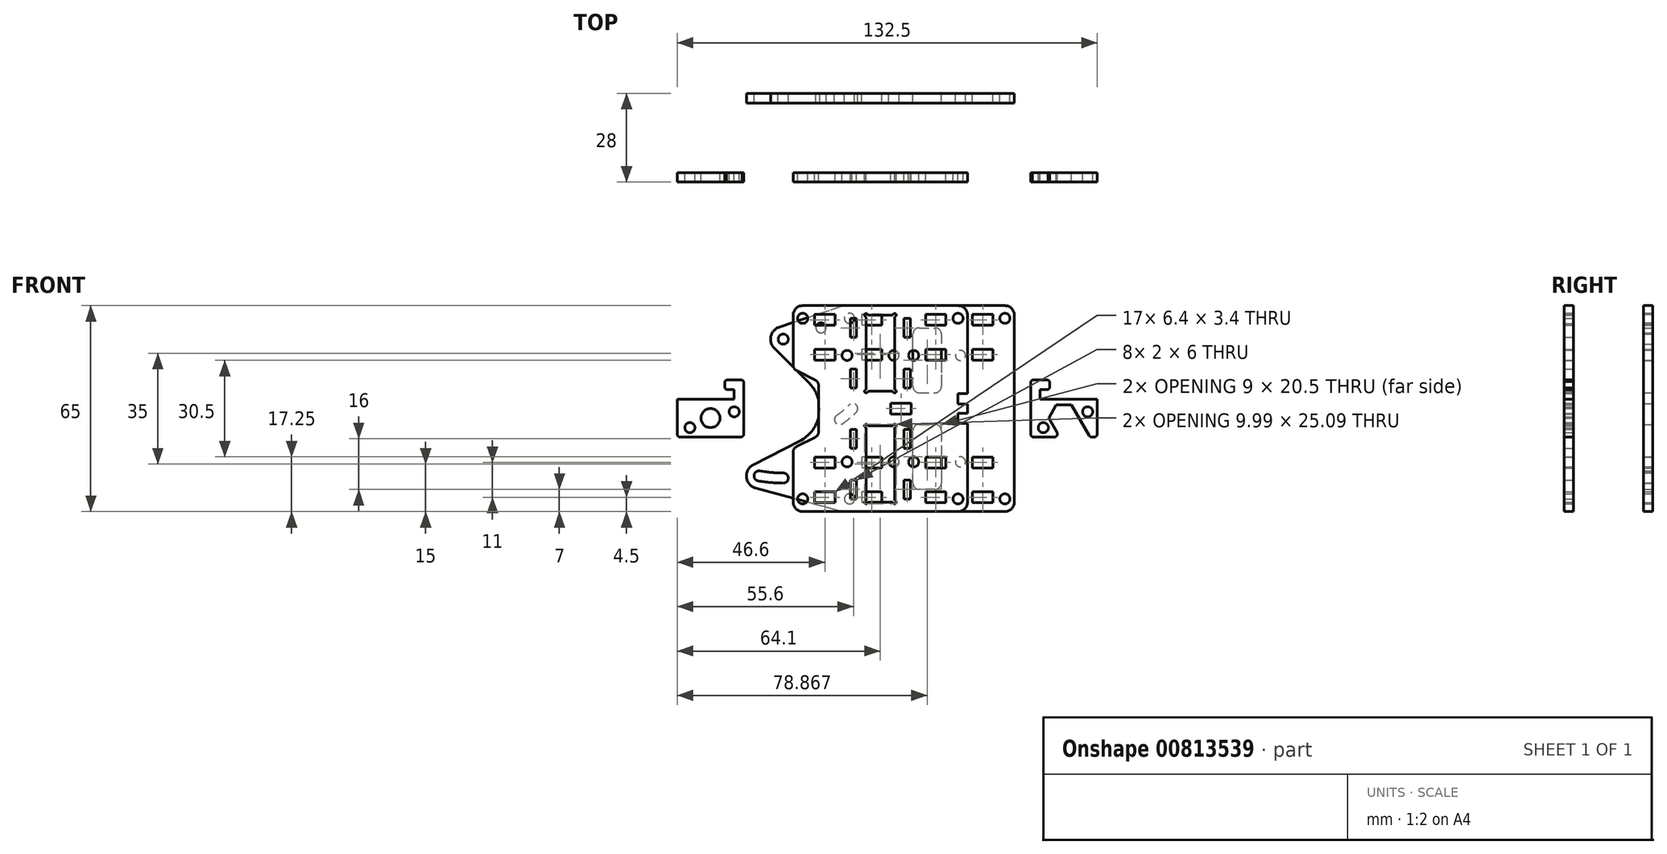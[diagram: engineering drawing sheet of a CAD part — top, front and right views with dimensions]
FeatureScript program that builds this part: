
annotation { "Feature Type Name" : "Feature", "Feature Type Description" : "" }
export const myFeature = defineFeature(function(context is Context, id is Id, definition is map)
    precondition{}
    {
        {
            var Q0;
            Q0=qCreatedBy(makeId("Front.planeOp"),FACE);
            var sketch = newSketch(context, id + "F0", { "sketchPlane" : qUnion([Q0])});
            skLineSegment(sketch, "E0", {"start": v(-7.5, 12.5) * mm, "end": v(-9.5, 12.5) * mm});
            skLineSegment(sketch, "E1", {"start": v(9.5, 12.5) * mm, "end": v(7.5, 12.5) * mm});
            skLineSegment(sketch, "E2", {"start": v(-9.5, -12.5) * mm, "end": v(-7.5, -12.5) * mm});
            skLineSegment(sketch, "E3", {"start": v(7.5, -12.5) * mm, "end": v(9.5, -12.5) * mm});
            skLineSegment(sketch, "E4", {"start": v(-7.5, -22.5) * mm, "end": v(-9.5, -22.5) * mm});
            skLineSegment(sketch, "E5", {"start": v(9.5, -22.5) * mm, "end": v(7.5, -22.5) * mm});
            skLineSegment(sketch, "E6", {"start": v(-9.5, 22.5) * mm, "end": v(-7.5, 22.5) * mm});
            skLineSegment(sketch, "E7", {"start": v(7.5, 22.5) * mm, "end": v(9.5, 22.5) * mm});
            skLineSegment(sketch, "E8", {"start": v(27.5, 1.5) * mm, "end": v(27.5, -1.5) * mm});
            skArc(sketch, "E9", {"start": v(4.75, 29.12) * mm, "mid": v(4.85, 29.9) * mm, "end": v(4.07, 29.8) * mm});
            skArc(sketch, "E10", {"start": v(3.63, 29.55) * mm, "mid": v(3.88, 29.62) * mm, "end": v(4.07, 29.8) * mm});
            skArc(sketch, "E11", {"start": v(4.75, 29.12) * mm, "mid": v(4.57, 28.93) * mm, "end": v(4.5, 28.68) * mm});
            skLineSegment(sketch, "E12", {"start": v(4.5, 6.32) * mm, "end": v(4.5, 28.68) * mm});
            skArc(sketch, "E13", {"start": v(4.5, 6.32) * mm, "mid": v(4.57, 6.07) * mm, "end": v(4.75, 5.88) * mm});
            skArc(sketch, "E14", {"start": v(4.07, 5.2) * mm, "mid": v(4.85, 5.1) * mm, "end": v(4.75, 5.88) * mm});
            skArc(sketch, "E15", {"start": v(4.07, 5.2) * mm, "mid": v(3.88, 5.38) * mm, "end": v(3.63, 5.45) * mm});
            skLineSegment(sketch, "E16", {"start": v(-3.63, 5.45) * mm, "end": v(3.63, 5.45) * mm});
            skArc(sketch, "E17", {"start": v(-3.63, 5.45) * mm, "mid": v(-3.88, 5.38) * mm, "end": v(-4.07, 5.2) * mm});
            skArc(sketch, "E18", {"start": v(-4.75, 5.88) * mm, "mid": v(-4.85, 5.1) * mm, "end": v(-4.07, 5.2) * mm});
            skArc(sketch, "E19", {"start": v(-4.75, 5.88) * mm, "mid": v(-4.57, 6.07) * mm, "end": v(-4.5, 6.32) * mm});
            skLineSegment(sketch, "E20", {"start": v(-4.5, 28.68) * mm, "end": v(-4.5, 6.32) * mm});
            skArc(sketch, "E21", {"start": v(-4.5, 28.68) * mm, "mid": v(-4.57, 28.93) * mm, "end": v(-4.75, 29.12) * mm});
            skArc(sketch, "E22", {"start": v(-4.07, 29.8) * mm, "mid": v(-4.85, 29.9) * mm, "end": v(-4.75, 29.12) * mm});
            skArc(sketch, "E23", {"start": v(-4.07, 29.8) * mm, "mid": v(-3.88, 29.62) * mm, "end": v(-3.63, 29.55) * mm});
            skLineSegment(sketch, "E24", {"start": v(3.63, 29.55) * mm, "end": v(-3.63, 29.55) * mm});
            skArc(sketch, "E25", {"start": v(4.75, -5.88) * mm, "mid": v(4.85, -5.1) * mm, "end": v(4.07, -5.2) * mm});
            skArc(sketch, "E26", {"start": v(3.63, -5.45) * mm, "mid": v(3.88, -5.38) * mm, "end": v(4.07, -5.2) * mm});
            skArc(sketch, "E27", {"start": v(4.75, -5.88) * mm, "mid": v(4.57, -6.07) * mm, "end": v(4.5, -6.32) * mm});
            skLineSegment(sketch, "E28", {"start": v(4.5, -28.68) * mm, "end": v(4.5, -6.32) * mm});
            skArc(sketch, "E29", {"start": v(4.5, -28.68) * mm, "mid": v(4.57, -28.93) * mm, "end": v(4.75, -29.12) * mm});
            skArc(sketch, "E30", {"start": v(4.07, -29.8) * mm, "mid": v(4.85, -29.9) * mm, "end": v(4.75, -29.12) * mm});
            skArc(sketch, "E31", {"start": v(4.07, -29.8) * mm, "mid": v(3.88, -29.62) * mm, "end": v(3.63, -29.55) * mm});
            skLineSegment(sketch, "E32", {"start": v(-3.63, -29.55) * mm, "end": v(3.63, -29.55) * mm});
            skArc(sketch, "E33", {"start": v(-3.63, -29.55) * mm, "mid": v(-3.88, -29.62) * mm, "end": v(-4.07, -29.8) * mm});
            skArc(sketch, "E34", {"start": v(-4.75, -29.12) * mm, "mid": v(-4.85, -29.9) * mm, "end": v(-4.07, -29.8) * mm});
            skArc(sketch, "E35", {"start": v(-4.75, -29.12) * mm, "mid": v(-4.57, -28.93) * mm, "end": v(-4.5, -28.68) * mm});
            skLineSegment(sketch, "E36", {"start": v(-4.5, -6.32) * mm, "end": v(-4.5, -28.68) * mm});
            skArc(sketch, "E37", {"start": v(-4.5, -6.32) * mm, "mid": v(-4.57, -6.07) * mm, "end": v(-4.75, -5.88) * mm});
            skArc(sketch, "E38", {"start": v(-4.07, -5.2) * mm, "mid": v(-4.85, -5.1) * mm, "end": v(-4.75, -5.88) * mm});
            skArc(sketch, "E39", {"start": v(-4.07, -5.2) * mm, "mid": v(-3.88, -5.38) * mm, "end": v(-3.63, -5.45) * mm});
            skLineSegment(sketch, "E40", {"start": v(3.63, -5.45) * mm, "end": v(-3.63, -5.45) * mm});
            skLineSegment(sketch, "E41", {"start": v(24.4, 1.5) * mm, "end": v(27.5, 1.5) * mm});
            skLineSegment(sketch, "E42", {"start": v(27.5, -1.5) * mm, "end": v(24.4, -1.5) * mm});
            skLineSegment(sketch, "E43", {"start": v(27.5, 4.7) * mm, "end": v(24.4, 4.7) * mm});
            skLineSegment(sketch, "E44", {"start": v(24.4, 4.7) * mm, "end": v(24.4, 1.5) * mm});
            skLineSegment(sketch, "E45", {"start": v(24.4, -4.7) * mm, "end": v(27.5, -4.7) * mm});
            skLineSegment(sketch, "E46", {"start": v(24.4, -1.5) * mm, "end": v(24.4, -4.7) * mm});
            skLineSegment(sketch, "E47", {"start": v(9.7, -1.7) * mm, "end": v(9.7, 1.7) * mm});
            skLineSegment(sketch, "E48", {"start": v(9.7, 1.7) * mm, "end": v(3.3, 1.7) * mm});
            skLineSegment(sketch, "E49", {"start": v(9.7, -1.7) * mm, "end": v(3.3, -1.7) * mm});
            skLineSegment(sketch, "E50", {"start": v(3.3, 1.7) * mm, "end": v(3.3, -1.7) * mm});
            skLineSegment(sketch, "E51", {"start": v(9.5, 28.5) * mm, "end": v(7.5, 28.5) * mm});
            skLineSegment(sketch, "E52", {"start": v(7.5, 6.5) * mm, "end": v(9.5, 6.5) * mm});
            skLineSegment(sketch, "E53", {"start": v(9.5, -6.5) * mm, "end": v(7.5, -6.5) * mm});
            skLineSegment(sketch, "E54", {"start": v(7.5, -28.5) * mm, "end": v(9.5, -28.5) * mm});
            skLineSegment(sketch, "E55", {"start": v(-7.5, 28.5) * mm, "end": v(-9.5, 28.5) * mm});
            skLineSegment(sketch, "E56", {"start": v(-9.5, 6.5) * mm, "end": v(-7.5, 6.5) * mm});
            skLineSegment(sketch, "E57", {"start": v(-7.5, -6.5) * mm, "end": v(-9.5, -6.5) * mm});
            skLineSegment(sketch, "E58", {"start": v(-9.5, -28.5) * mm, "end": v(-7.5, -28.5) * mm});
            skLineSegment(sketch, "E59", {"start": v(9.5, 22.5) * mm, "end": v(9.5, 28.5) * mm});
            skLineSegment(sketch, "E60", {"start": v(7.5, 28.5) * mm, "end": v(7.5, 22.5) * mm});
            skLineSegment(sketch, "E61", {"start": v(9.5, 6.5) * mm, "end": v(9.5, 12.5) * mm});
            skLineSegment(sketch, "E62", {"start": v(7.5, 12.5) * mm, "end": v(7.5, 6.5) * mm});
            skLineSegment(sketch, "E63", {"start": v(9.5, -12.5) * mm, "end": v(9.5, -6.5) * mm});
            skLineSegment(sketch, "E64", {"start": v(7.5, -6.5) * mm, "end": v(7.5, -12.5) * mm});
            skLineSegment(sketch, "E65", {"start": v(9.5, -28.5) * mm, "end": v(9.5, -22.5) * mm});
            skLineSegment(sketch, "E66", {"start": v(7.5, -22.5) * mm, "end": v(7.5, -28.5) * mm});
            skLineSegment(sketch, "E67", {"start": v(-7.5, 22.5) * mm, "end": v(-7.5, 28.5) * mm});
            skLineSegment(sketch, "E68", {"start": v(-9.5, 28.5) * mm, "end": v(-9.5, 22.5) * mm});
            skLineSegment(sketch, "E69", {"start": v(-7.5, 6.5) * mm, "end": v(-7.5, 12.5) * mm});
            skLineSegment(sketch, "E70", {"start": v(-9.5, 12.5) * mm, "end": v(-9.5, 6.5) * mm});
            skLineSegment(sketch, "E71", {"start": v(-7.5, -12.5) * mm, "end": v(-7.5, -6.5) * mm});
            skLineSegment(sketch, "E72", {"start": v(-9.5, -6.5) * mm, "end": v(-9.5, -12.5) * mm});
            skLineSegment(sketch, "E73", {"start": v(-7.5, -28.5) * mm, "end": v(-7.5, -22.5) * mm});
            skLineSegment(sketch, "E74", {"start": v(-9.5, -22.5) * mm, "end": v(-9.5, -28.5) * mm});
            skLineSegment(sketch, "E75", {"start": v(-14.3, 26.3) * mm, "end": v(-14.3, 29.7) * mm});
            skLineSegment(sketch, "E76", {"start": v(-14.3, 29.7) * mm, "end": v(-20.7, 29.7) * mm});
            skLineSegment(sketch, "E77", {"start": v(-14.3, 26.3) * mm, "end": v(-20.7, 26.3) * mm});
            skLineSegment(sketch, "E78", {"start": v(-20.7, 29.7) * mm, "end": v(-20.7, 26.3) * mm});
            skLineSegment(sketch, "E79", {"start": v(-14.3, 15.3) * mm, "end": v(-14.3, 18.7) * mm});
            skLineSegment(sketch, "E80", {"start": v(-14.3, 18.7) * mm, "end": v(-20.7, 18.7) * mm});
            skLineSegment(sketch, "E81", {"start": v(-14.3, 15.3) * mm, "end": v(-20.7, 15.3) * mm});
            skLineSegment(sketch, "E82", {"start": v(-20.7, 18.7) * mm, "end": v(-20.7, 15.3) * mm});
            skLineSegment(sketch, "E83", {"start": v(-14.3, -18.7) * mm, "end": v(-14.3, -15.3) * mm});
            skLineSegment(sketch, "E84", {"start": v(-14.3, -15.3) * mm, "end": v(-20.7, -15.3) * mm});
            skLineSegment(sketch, "E85", {"start": v(-14.3, -18.7) * mm, "end": v(-20.7, -18.7) * mm});
            skLineSegment(sketch, "E86", {"start": v(-20.7, -15.3) * mm, "end": v(-20.7, -18.7) * mm});
            skLineSegment(sketch, "E87", {"start": v(-14.3, -29.7) * mm, "end": v(-14.3, -26.3) * mm});
            skLineSegment(sketch, "E88", {"start": v(-14.3, -26.3) * mm, "end": v(-20.7, -26.3) * mm});
            skLineSegment(sketch, "E89", {"start": v(-14.3, -29.7) * mm, "end": v(-20.7, -29.7) * mm});
            skLineSegment(sketch, "E90", {"start": v(-20.7, -26.3) * mm, "end": v(-20.7, -29.7) * mm});
            skCircle(sketch, "E91", {"center": v(-24.5, 28.5) * mm, "radius": 1.6 * mm});
            skCircle(sketch, "E92", {"center": v(-24.5, -28.5) * mm, "radius": 1.6 * mm});
            skLineSegment(sketch, "E93", {"start": v(20.7, 26.3) * mm, "end": v(20.7, 29.7) * mm});
            skLineSegment(sketch, "E94", {"start": v(20.7, 29.7) * mm, "end": v(14.3, 29.7) * mm});
            skLineSegment(sketch, "E95", {"start": v(20.7, 26.3) * mm, "end": v(14.3, 26.3) * mm});
            skLineSegment(sketch, "E96", {"start": v(14.3, 29.7) * mm, "end": v(14.3, 26.3) * mm});
            skLineSegment(sketch, "E97", {"start": v(20.7, 15.3) * mm, "end": v(20.7, 18.7) * mm});
            skLineSegment(sketch, "E98", {"start": v(20.7, 18.7) * mm, "end": v(14.3, 18.7) * mm});
            skLineSegment(sketch, "E99", {"start": v(20.7, 15.3) * mm, "end": v(14.3, 15.3) * mm});
            skLineSegment(sketch, "E100", {"start": v(14.3, 18.7) * mm, "end": v(14.3, 15.3) * mm});
            skLineSegment(sketch, "E101", {"start": v(20.7, -18.7) * mm, "end": v(20.7, -15.3) * mm});
            skLineSegment(sketch, "E102", {"start": v(20.7, -15.3) * mm, "end": v(14.3, -15.3) * mm});
            skLineSegment(sketch, "E103", {"start": v(20.7, -18.7) * mm, "end": v(14.3, -18.7) * mm});
            skLineSegment(sketch, "E104", {"start": v(14.3, -15.3) * mm, "end": v(14.3, -18.7) * mm});
            skLineSegment(sketch, "E105", {"start": v(20.7, -29.7) * mm, "end": v(20.7, -26.3) * mm});
            skLineSegment(sketch, "E106", {"start": v(20.7, -26.3) * mm, "end": v(14.3, -26.3) * mm});
            skLineSegment(sketch, "E107", {"start": v(20.7, -29.7) * mm, "end": v(14.3, -29.7) * mm});
            skLineSegment(sketch, "E108", {"start": v(14.3, -26.3) * mm, "end": v(14.3, -29.7) * mm});
            skCircle(sketch, "E109", {"center": v(24.5, 28.5) * mm, "radius": 1.6 * mm});
            skCircle(sketch, "E110", {"center": v(24.5, -28.5) * mm, "radius": 1.6 * mm});
            skLineSegment(sketch, "E111", {"start": v(27.5, -4.7) * mm, "end": v(27.5, -29.5) * mm});
            skArc(sketch, "E112", {"start": v(24.5, -32.5) * mm, "mid": v(26.62, -31.62) * mm, "end": v(27.5, -29.5) * mm});
            skArc(sketch, "E113", {"start": v(27.5, 29.5) * mm, "mid": v(26.62, 31.62) * mm, "end": v(24.5, 32.5) * mm});
            skCircle(sketch, "E114", {"center": v(-10.5, 16.8) * mm, "radius": 1.6 * mm});
            skCircle(sketch, "E115", {"center": v(10.5, 16.8) * mm, "radius": 1.6 * mm});
            skCircle(sketch, "E116", {"center": v(10.5, -16.8) * mm, "radius": 1.6 * mm});
            skCircle(sketch, "E117", {"center": v(-10.5, -16.8) * mm, "radius": 1.6 * mm});
            skLineSegment(sketch, "E118", {"start": v(-24.5, 32.5) * mm, "end": v(24.5, 32.5) * mm});
            skLineSegment(sketch, "E119", {"start": v(24.5, -32.5) * mm, "end": v(-24.5, -32.5) * mm});
            skArc(sketch, "E120", {"start": v(-27.5, 13.74) * mm, "mid": v(-27.2, 12.68) * mm, "end": v(-26.4, 11.95) * mm});
            skLineSegment(sketch, "E121", {"start": v(-26.4, 11.95) * mm, "end": v(-20.6, 9.05) * mm});
            skArc(sketch, "E122", {"start": v(-19.5, 7.26) * mm, "mid": v(-19.8, 8.32) * mm, "end": v(-20.6, 9.05) * mm});
            skLineSegment(sketch, "E123", {"start": v(-19.5, 7.26) * mm, "end": v(-19.5, -7.26) * mm});
            skArc(sketch, "E124", {"start": v(-20.6, -9.05) * mm, "mid": v(-19.8, -8.32) * mm, "end": v(-19.5, -7.26) * mm});
            skLineSegment(sketch, "E125", {"start": v(-20.6, -9.05) * mm, "end": v(-26.4, -11.95) * mm});
            skArc(sketch, "E126", {"start": v(-26.4, -11.95) * mm, "mid": v(-27.2, -12.68) * mm, "end": v(-27.5, -13.74) * mm});
            skLineSegment(sketch, "E127", {"start": v(-27.5, 29.5) * mm, "end": v(-27.5, 13.74) * mm});
            skArc(sketch, "E128", {"start": v(-24.5, 32.5) * mm, "mid": v(-26.62, 31.62) * mm, "end": v(-27.5, 29.5) * mm});
            skLineSegment(sketch, "E129", {"start": v(-27.5, -13.74) * mm, "end": v(-27.5, -29.5) * mm});
            skArc(sketch, "E130", {"start": v(-27.5, -29.5) * mm, "mid": v(-26.62, -31.62) * mm, "end": v(-24.5, -32.5) * mm});
            skLineSegment(sketch, "E131", {"start": v(27.5, 29.5) * mm, "end": v(27.5, 4.7) * mm});
            skSolve(sketch);
        }
        {
            var Q0;
            Q0=makeQuery(id+"F0.imprint","IMPRINT",FACE,{"disambiguationData":[TD([[makeQuery(id+"F0.imprint","IMPRINT",EDGE,{"derivedFrom":sQuery(id+"F0.wireOp",EDGE,"E0")}),-1.0]])]});
            extrude(context, id + "F1", {"entities" : qUnion([Q0]), "depth" : 3 * mm, "offsetDistance" : 25 * mm});
        }
        {
            var Q0;
            Q0=qCreatedBy(makeId("Front.planeOp"),FACE);
            cPlane(context, id + "F2", {"entities" : qUnion([Q0]), "cplaneType" : CPlaneType.OFFSET, "offset" : 25 * mm, "oppositeDirection" : true, "width" : 150 * mm, "height" : 150 * mm});
        }
        {
            var Q0;
            Q0=qCreatedBy(id+"F2.planeOp",FACE);
            var sketch = newSketch(context, id + "F3", { "sketchPlane" : qUnion([Q0])});
            skArc(sketch, "E132", {"start": v(19.27, 23.5) * mm, "mid": v(18.68, 24.91) * mm, "end": v(17.27, 25.5) * mm});
            skLineSegment(sketch, "E133", {"start": v(12.27, 25.5) * mm, "end": v(17.27, 25.5) * mm});
            skArc(sketch, "E134", {"start": v(12.27, 25.5) * mm, "mid": v(10.85, 24.91) * mm, "end": v(10.27, 23.5) * mm});
            skArc(sketch, "E135", {"start": v(17.27, -25.5) * mm, "mid": v(18.68, -24.91) * mm, "end": v(19.27, -23.5) * mm});
            skLineSegment(sketch, "E136", {"start": v(17.27, -25.5) * mm, "end": v(12.27, -25.5) * mm});
            skArc(sketch, "E137", {"start": v(10.27, -23.5) * mm, "mid": v(10.85, -24.91) * mm, "end": v(12.27, -25.5) * mm});
            skLineSegment(sketch, "E138", {"start": v(10.27, 7) * mm, "end": v(10.27, 23.5) * mm});
            skArc(sketch, "E139", {"start": v(10.27, 7) * mm, "mid": v(10.85, 5.59) * mm, "end": v(12.27, 5) * mm});
            skLineSegment(sketch, "E140", {"start": v(19.27, 23.5) * mm, "end": v(19.27, 7) * mm});
            skLineSegment(sketch, "E141", {"start": v(12.27, 5) * mm, "end": v(17.27, 5) * mm});
            skArc(sketch, "E142", {"start": v(17.27, 5) * mm, "mid": v(18.68, 5.59) * mm, "end": v(19.27, 7) * mm});
            skLineSegment(sketch, "E143", {"start": v(10.27, -23.5) * mm, "end": v(10.27, -7) * mm});
            skArc(sketch, "E144", {"start": v(12.27, -5) * mm, "mid": v(10.85, -5.59) * mm, "end": v(10.27, -7) * mm});
            skLineSegment(sketch, "E145", {"start": v(12.27, -5) * mm, "end": v(17.27, -5) * mm});
            skLineSegment(sketch, "E146", {"start": v(19.27, -7) * mm, "end": v(19.27, -23.5) * mm});
            skArc(sketch, "E147", {"start": v(19.27, -7) * mm, "mid": v(18.68, -5.59) * mm, "end": v(17.27, -5) * mm});
            skCircle(sketch, "E148", {"center": v(-9.73, 28.5) * mm, "radius": 1.6 * mm});
            skCircle(sketch, "E149", {"center": v(-9.73, -28.5) * mm, "radius": 1.6 * mm});
            skLineSegment(sketch, "E150", {"start": v(0.47, 26.3) * mm, "end": v(0.47, 29.7) * mm});
            skLineSegment(sketch, "E151", {"start": v(0.47, 29.7) * mm, "end": v(-5.93, 29.7) * mm});
            skLineSegment(sketch, "E152", {"start": v(0.47, 26.3) * mm, "end": v(-5.93, 26.3) * mm});
            skLineSegment(sketch, "E153", {"start": v(-5.93, 29.7) * mm, "end": v(-5.93, 26.3) * mm});
            skLineSegment(sketch, "E154", {"start": v(0.47, 15.3) * mm, "end": v(0.47, 18.7) * mm});
            skLineSegment(sketch, "E155", {"start": v(0.47, 18.7) * mm, "end": v(-5.93, 18.7) * mm});
            skLineSegment(sketch, "E156", {"start": v(0.47, 15.3) * mm, "end": v(-5.93, 15.3) * mm});
            skLineSegment(sketch, "E157", {"start": v(-5.93, 18.7) * mm, "end": v(-5.93, 15.3) * mm});
            skLineSegment(sketch, "E158", {"start": v(0.47, -18.7) * mm, "end": v(0.47, -15.3) * mm});
            skLineSegment(sketch, "E159", {"start": v(0.47, -15.3) * mm, "end": v(-5.93, -15.3) * mm});
            skLineSegment(sketch, "E160", {"start": v(0.47, -18.7) * mm, "end": v(-5.93, -18.7) * mm});
            skLineSegment(sketch, "E161", {"start": v(-5.93, -15.3) * mm, "end": v(-5.93, -18.7) * mm});
            skLineSegment(sketch, "E162", {"start": v(0.47, -29.7) * mm, "end": v(0.47, -26.3) * mm});
            skLineSegment(sketch, "E163", {"start": v(0.47, -26.3) * mm, "end": v(-5.93, -26.3) * mm});
            skLineSegment(sketch, "E164", {"start": v(0.47, -29.7) * mm, "end": v(-5.93, -29.7) * mm});
            skLineSegment(sketch, "E165", {"start": v(-5.93, -26.3) * mm, "end": v(-5.93, -29.7) * mm});
            skCircle(sketch, "E166", {"center": v(-30.65, 21.92) * mm, "radius": 1.6 * mm});
            skArc(sketch, "E167", {"start": v(-7.6, -1.13) * mm, "mid": v(-7.6, 1.13) * mm, "end": v(-9.86, 1.13) * mm});
            skArc(sketch, "E168", {"start": v(-13.8, -2.16) * mm, "mid": v(-11.76, -0.6) * mm, "end": v(-9.86, 1.13) * mm});
            skArc(sketch, "E169", {"start": v(-11.96, -4.78) * mm, "mid": v(-9.7, -3.05) * mm, "end": v(-7.6, -1.13) * mm});
            skArc(sketch, "E170", {"start": v(-13.8, -2.16) * mm, "mid": v(-14.18, -4.4) * mm, "end": v(-11.96, -4.78) * mm});
            skArc(sketch, "E171", {"start": v(-37.99, -19.68) * mm, "mid": v(-34.34, -20.16) * mm, "end": v(-30.65, -20.32) * mm});
            skArc(sketch, "E172", {"start": v(-30.65, -23.52) * mm, "mid": v(-29.05, -21.92) * mm, "end": v(-30.65, -20.32) * mm});
            skArc(sketch, "E173", {"start": v(-38.54, -22.83) * mm, "mid": v(-34.61, -23.35) * mm, "end": v(-30.65, -23.52) * mm});
            skArc(sketch, "E174", {"start": v(-37.99, -19.68) * mm, "mid": v(-39.84, -20.98) * mm, "end": v(-38.54, -22.83) * mm});
            skCircle(sketch, "E175", {"center": v(-18.73, 25.5) * mm, "radius": 1.6 * mm});
            skLineSegment(sketch, "E176", {"start": v(-33.48, 19.1) * mm, "end": v(-22.52, 8.13) * mm});
            skLineSegment(sketch, "E177", {"start": v(-40.08, -17.69) * mm, "end": v(-25.44, -10.25) * mm});
            skArc(sketch, "E178", {"start": v(-31.93, 25.71) * mm, "mid": v(-34.55, 22.83) * mm, "end": v(-33.48, 19.1) * mm});
            skArc(sketch, "E179", {"start": v(-40.08, -17.69) * mm, "mid": v(-42.24, -21.67) * mm, "end": v(-39.3, -25.12) * mm});
            skArc(sketch, "E180", {"start": v(-25.44, -10.25) * mm, "mid": v(-19.3, -1.8) * mm, "end": v(-22.52, 8.13) * mm});
            skLineSegment(sketch, "E181", {"start": v(-39.3, -25.12) * mm, "end": v(-12.24, -32.36) * mm});
            skArc(sketch, "E182", {"start": v(-12.24, -32.36) * mm, "mid": v(-11.73, -32.47) * mm, "end": v(-11.2, -32.5) * mm});
            skLineSegment(sketch, "E183", {"start": v(-31.93, 25.71) * mm, "end": v(-12.35, 32.3) * mm});
            skArc(sketch, "E184", {"start": v(-11.08, 32.5) * mm, "mid": v(-11.72, 32.45) * mm, "end": v(-12.35, 32.3) * mm});
            skCircle(sketch, "E185", {"center": v(39.27, 28.5) * mm, "radius": 1.6 * mm});
            skCircle(sketch, "E186", {"center": v(39.27, -28.5) * mm, "radius": 1.6 * mm});
            skLineSegment(sketch, "E187", {"start": v(35.47, 26.3) * mm, "end": v(35.47, 29.7) * mm});
            skLineSegment(sketch, "E188", {"start": v(35.47, 29.7) * mm, "end": v(29.07, 29.7) * mm});
            skLineSegment(sketch, "E189", {"start": v(35.47, 26.3) * mm, "end": v(29.07, 26.3) * mm});
            skLineSegment(sketch, "E190", {"start": v(29.07, 29.7) * mm, "end": v(29.07, 26.3) * mm});
            skLineSegment(sketch, "E191", {"start": v(35.47, 15.3) * mm, "end": v(35.47, 18.7) * mm});
            skLineSegment(sketch, "E192", {"start": v(35.47, 18.7) * mm, "end": v(29.07, 18.7) * mm});
            skLineSegment(sketch, "E193", {"start": v(35.47, 15.3) * mm, "end": v(29.07, 15.3) * mm});
            skLineSegment(sketch, "E194", {"start": v(29.07, 18.7) * mm, "end": v(29.07, 15.3) * mm});
            skLineSegment(sketch, "E195", {"start": v(35.47, -18.7) * mm, "end": v(35.47, -15.3) * mm});
            skLineSegment(sketch, "E196", {"start": v(35.47, -15.3) * mm, "end": v(29.07, -15.3) * mm});
            skLineSegment(sketch, "E197", {"start": v(35.47, -18.7) * mm, "end": v(29.07, -18.7) * mm});
            skLineSegment(sketch, "E198", {"start": v(29.07, -15.3) * mm, "end": v(29.07, -18.7) * mm});
            skLineSegment(sketch, "E199", {"start": v(35.47, -29.7) * mm, "end": v(35.47, -26.3) * mm});
            skLineSegment(sketch, "E200", {"start": v(35.47, -26.3) * mm, "end": v(29.07, -26.3) * mm});
            skLineSegment(sketch, "E201", {"start": v(35.47, -29.7) * mm, "end": v(29.07, -29.7) * mm});
            skLineSegment(sketch, "E202", {"start": v(29.07, -26.3) * mm, "end": v(29.07, -29.7) * mm});
            skLineSegment(sketch, "E203", {"start": v(-11.08, 32.5) * mm, "end": v(39.27, 32.5) * mm});
            skArc(sketch, "E204", {"start": v(42.27, 29.5) * mm, "mid": v(41.39, 31.62) * mm, "end": v(39.27, 32.5) * mm});
            skLineSegment(sketch, "E205", {"start": v(39.27, -32.5) * mm, "end": v(-11.2, -32.5) * mm});
            skLineSegment(sketch, "E206", {"start": v(42.27, 29.5) * mm, "end": v(42.27, -29.5) * mm});
            skArc(sketch, "E207", {"start": v(39.27, -32.5) * mm, "mid": v(41.39, -31.62) * mm, "end": v(42.27, -29.5) * mm});
            skCircle(sketch, "E208", {"center": v(25.27, 16.8) * mm, "radius": 1.6 * mm});
            skCircle(sketch, "E209", {"center": v(4.27, 16.8) * mm, "radius": 1.6 * mm});
            skCircle(sketch, "E210", {"center": v(4.27, -16.8) * mm, "radius": 1.6 * mm});
            skCircle(sketch, "E211", {"center": v(25.27, -16.8) * mm, "radius": 1.6 * mm});
            skSolve(sketch);
        }
        {
            var Q0;
            Q0=makeQuery(id+"F3.imprint","IMPRINT",FACE,{"disambiguationData":[TD([[makeQuery(id+"F3.imprint","IMPRINT",EDGE,{"derivedFrom":sQuery(id+"F3.wireOp",EDGE,"E132")}),-1.0]])]});
            extrude(context, id + "F4", {"entities" : qUnion([Q0]), "depth" : 3 * mm, "offsetDistance" : 25 * mm});
        }
        {
            var Q0;
            Q0=makeQuery(id+"F1.opExtrude","CAP_EDGE",EDGE,{"disambiguationData":[OSD([sQuery(id+"F0.wireOp",EDGE,"E20")])],"isStart":true});
            cPoint(context, id + "F5", {"entities" : qUnion([Q0]), "parameter" : 0.5});
        }
        {
            var Q0;
            Q0=qCreatedBy(id+"F5",VERTEX);
            var Q1;
            Q1=makeQuery(id+"F1.opExtrude","CAP_EDGE",EDGE,{"disambiguationData":[OSD([sQuery(id+"F0.wireOp",EDGE,"E20")])],"isStart":true});
            cPlane(context, id + "F6", {"entities" : qUnion([Q0, Q1]), "cplaneType" : CPlaneType.LINE_POINT, "offset" : 25 * mm, "width" : 150 * mm, "height" : 150 * mm});
        }
        {
            var Q0;
            Q0=qCreatedBy(id+"F6.planeOp",FACE);
            var sketch = newSketch(context, id + "F7", { "sketchPlane" : qUnion([Q0])});
            skCircle(sketch, "E212", {"center": v(0, 9) * mm, "radius": 7.5 * mm, "construction": true});
            skSolve(sketch);
        }
        {
            var Q0;
            Q0=makeQuery(id+"F1.opExtrude","CAP_EDGE",EDGE,{"disambiguationData":[OSD([sQuery(id+"F0.wireOp",EDGE,"E36")])],"isStart":true});
            cPoint(context, id + "F8", {"entities" : qUnion([Q0]), "parameter" : 0.5});
        }
        {
            var Q0;
            Q0=qCreatedBy(id+"F8",VERTEX);
            var Q1;
            Q1=makeQuery(id+"F1.opExtrude","CAP_EDGE",EDGE,{"disambiguationData":[OSD([sQuery(id+"F0.wireOp",EDGE,"E36")])],"isStart":true});
            cPlane(context, id + "F9", {"entities" : qUnion([Q0, Q1]), "cplaneType" : CPlaneType.LINE_POINT, "offset" : 25 * mm, "width" : 150 * mm, "height" : 150 * mm});
        }
        {
            var Q0;
            Q0=qCreatedBy(id+"F9.planeOp",FACE);
            var sketch = newSketch(context, id + "F10", { "sketchPlane" : qUnion([Q0])});
            skCircle(sketch, "E213", {"center": v(0, 9) * mm, "radius": 7.5 * mm, "construction": true});
            skSolve(sketch);
        }
        {
            var Q0;
            Q0=qCreatedBy(makeId("Front.planeOp"),FACE);
            var sketch = newSketch(context, id + "F11", { "sketchPlane" : qUnion([Q0])});
            skLineSegment(sketch, "E214", {"start": v(-46.1, 6) * mm, "end": v(-46.1, 3) * mm});
            skLineSegment(sketch, "E215", {"start": v(-64.1, 3) * mm, "end": v(-46.1, 3) * mm});
            skLineSegment(sketch, "E216", {"start": v(-64.1, 3) * mm, "end": v(-64.1, -8) * mm});
            skArc(sketch, "E217", {"start": v(-64.1, -8) * mm, "mid": v(-63.8, -8.7) * mm, "end": v(-63.1, -9) * mm});
            skLineSegment(sketch, "E218", {"start": v(-63.1, -9) * mm, "end": v(-44.1, -9) * mm});
            skArc(sketch, "E219", {"start": v(-44.1, -9) * mm, "mid": v(-43.4, -8.7) * mm, "end": v(-43.1, -8) * mm});
            skCircle(sketch, "E220", {"center": v(-46.1, -1) * mm, "radius": 1.6 * mm});
            skCircle(sketch, "E221", {"center": v(-60.1, -6) * mm, "radius": 1.6 * mm});
            skCircle(sketch, "E222", {"center": v(-53.6, -3) * mm, "radius": 3 * mm});
            skLineSegment(sketch, "E223", {"start": v(-48.6, 9) * mm, "end": v(-49.1, 8.5) * mm});
            skLineSegment(sketch, "E224", {"start": v(-43.6, 9) * mm, "end": v(-48.6, 9) * mm});
            skLineSegment(sketch, "E225", {"start": v(-43.1, -8) * mm, "end": v(-43.1, 8.5) * mm});
            skLineSegment(sketch, "E226", {"start": v(-43.6, 9) * mm, "end": v(-43.1, 8.5) * mm});
            skLineSegment(sketch, "E227", {"start": v(-49.1, 8.5) * mm, "end": v(-49.1, 6.5) * mm});
            skLineSegment(sketch, "E228", {"start": v(-48.6, 6) * mm, "end": v(-46.1, 6) * mm});
            skLineSegment(sketch, "E229", {"start": v(-49.1, 6.5) * mm, "end": v(-48.6, 6) * mm});
            skLineSegment(sketch, "E230", {"start": v(50.4, 3) * mm, "end": v(50.4, 6) * mm});
            skLineSegment(sketch, "E231", {"start": v(53.1, -3) * mm, "end": v(55.5, 1.16) * mm});
            skLineSegment(sketch, "E232", {"start": v(55.5, 1.16) * mm, "end": v(60.3, 1.16) * mm});
            skLineSegment(sketch, "E233", {"start": v(50.4, 3) * mm, "end": v(68.4, 3) * mm});
            skArc(sketch, "E234", {"start": v(47.4, -8) * mm, "mid": v(47.7, -8.7) * mm, "end": v(48.4, -9) * mm});
            skLineSegment(sketch, "E235", {"start": v(48.4, -9) * mm, "end": v(54.83, -9) * mm});
            skLineSegment(sketch, "E236", {"start": v(53.1, -3) * mm, "end": v(55.7, -7.5) * mm});
            skArc(sketch, "E237", {"start": v(54.83, -9) * mm, "mid": v(55.7, -8.5) * mm, "end": v(55.7, -7.5) * mm});
            skLineSegment(sketch, "E238", {"start": v(60.3, 1.16) * mm, "end": v(65.88, -8.5) * mm});
            skArc(sketch, "E239", {"start": v(65.88, -8.5) * mm, "mid": v(66.24, -8.87) * mm, "end": v(66.74, -9) * mm});
            skLineSegment(sketch, "E240", {"start": v(66.74, -9) * mm, "end": v(67.4, -9) * mm});
            skLineSegment(sketch, "E241", {"start": v(68.4, -8) * mm, "end": v(68.4, 3) * mm});
            skArc(sketch, "E242", {"start": v(67.4, -9) * mm, "mid": v(68.1, -8.7) * mm, "end": v(68.4, -8) * mm});
            skCircle(sketch, "E243", {"center": v(65.4, -1) * mm, "radius": 1.6 * mm});
            skCircle(sketch, "E244", {"center": v(51.4, -6) * mm, "radius": 1.6 * mm});
            skLineSegment(sketch, "E245", {"start": v(53.4, 8.5) * mm, "end": v(52.9, 9) * mm});
            skLineSegment(sketch, "E246", {"start": v(47.9, 9) * mm, "end": v(52.9, 9) * mm});
            skLineSegment(sketch, "E247", {"start": v(47.4, -8) * mm, "end": v(47.4, 8.5) * mm});
            skLineSegment(sketch, "E248", {"start": v(47.9, 9) * mm, "end": v(47.4, 8.5) * mm});
            skLineSegment(sketch, "E249", {"start": v(53.4, 8.5) * mm, "end": v(53.4, 6.5) * mm});
            skLineSegment(sketch, "E250", {"start": v(52.9, 6) * mm, "end": v(50.4, 6) * mm});
            skLineSegment(sketch, "E251", {"start": v(53.4, 6.5) * mm, "end": v(52.9, 6) * mm});
            skSolve(sketch);
        }
        {
            var Q0;
            Q0=makeQuery(id+"F11.imprint","IMPRINT",FACE,{"disambiguationData":[TD([[makeQuery(id+"F11.imprint","IMPRINT",EDGE,{"derivedFrom":sQuery(id+"F11.wireOp",EDGE,"E230")}),1.0]])]});
            var Q1;
            Q1=makeQuery(id+"F11.imprint","IMPRINT",FACE,{"disambiguationData":[TD([[makeQuery(id+"F11.imprint","IMPRINT",EDGE,{"derivedFrom":sQuery(id+"F11.wireOp",EDGE,"E214")}),1.0]])]});
            extrude(context, id + "F12", {"entities" : qUnion([Q0, Q1]), "depth" : 3 * mm, "offsetDistance" : 25 * mm});
        }
    });
